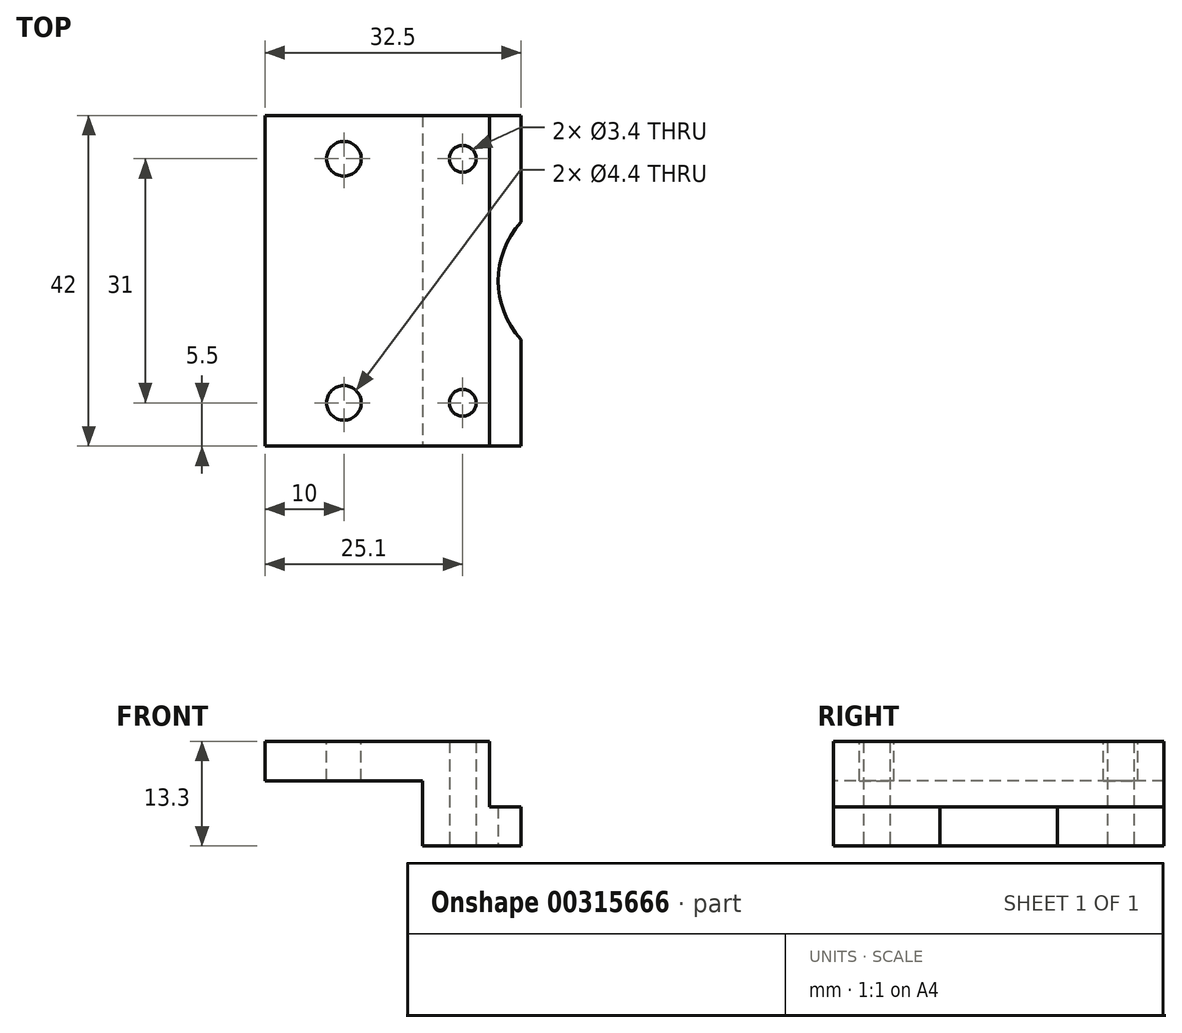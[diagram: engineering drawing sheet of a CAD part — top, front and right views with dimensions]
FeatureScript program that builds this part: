
annotation { "Feature Type Name" : "Feature", "Feature Type Description" : "" }
export const myFeature = defineFeature(function(context is Context, id is Id, definition is map)
    precondition{}
    {
        {
            var Q0;
            Q0=qCreatedBy(makeId("Front.planeOp"),FACE);
            var sketch = newSketch(context, id + "F0", { "sketchPlane" : qUnion([Q0])});
            skLineSegment(sketch, "E0", {"start": v(8.5, 13.3) * mm, "end": v(8.5, 5) * mm});
            skLineSegment(sketch, "E1", {"start": v(8.5, 5) * mm, "end": v(12.5, 5) * mm});
            skLineSegment(sketch, "E2", {"start": v(12.5, 5) * mm, "end": v(12.5, 0) * mm});
            skLineSegment(sketch, "E3", {"start": v(12.5, 0) * mm, "end": v(0, 0) * mm});
            skLineSegment(sketch, "E4", {"start": v(0, 0) * mm, "end": v(0, 13.3) * mm});
            skLineSegment(sketch, "E5", {"start": v(0, 13.3) * mm, "end": v(8.5, 13.3) * mm});
            skSolve(sketch);
        }
        {
            var Q0;
            Q0=qSketchRegion(id+"F0",true);
            extrude(context, id + "F1", {"entities" : qUnion([Q0]), "oppositeDirection" : true, "depth" : 42 * mm});
        }
        {
            var Q0;
            Q0=makeQuery(id+"F1.opExtrude","SWEPT_FACE",FACE,{"disambiguationData":[OSD([sQuery(id+"F0.wireOp",EDGE,"E3")])]});
            var sketch = newSketch(context, id + "F2", { "sketchPlane" : qUnion([Q0])});
            skCircle(sketch, "E6", {"center": v(5.1, -5.5) * mm, "radius": 1.7 * mm});
            skCircle(sketch, "E7", {"center": v(5.1, -36.5) * mm, "radius": 1.7 * mm});
            skCircle(sketch, "E8", {"center": v(20.6, -21) * mm, "radius": 11 * mm});
            skLineSegment(sketch, "E9", {"start": v(0, -21) * mm, "end": v(12.5, -21) * mm, "construction": true});
            skSolve(sketch);
        }
        {
            var Q0;
            Q0=qSketchRegion(id+"F2",true);
            extrude(context, id + "F3", {"entities" : qUnion([Q0]), "operationType" : NewBodyOperationType.REMOVE, "endBound" : BoundingType.THROUGH_ALL, "oppositeDirection" : true, "depth" : 25 * mm});
        }
        {
            var Q0;
            Q0=makeQuery(id+"F1.opExtrude","SWEPT_FACE",FACE,{"disambiguationData":[OSD([sQuery(id+"F0.wireOp",EDGE,"E4")])]});
            var sketch = newSketch(context, id + "F4", { "sketchPlane" : qUnion([Q0])});
            skLineSegment(sketch, "E10.bottom", {"start": v(-42, 13.3) * mm, "end": v(0, 13.3) * mm});
            skLineSegment(sketch, "E10.top", {"start": v(-42, 8.3) * mm, "end": v(0, 8.3) * mm});
            skLineSegment(sketch, "E10.left", {"start": v(-42, 13.3) * mm, "end": v(-42, 8.3) * mm});
            skLineSegment(sketch, "E10.right", {"start": v(0, 13.3) * mm, "end": v(0, 8.3) * mm});
            skSolve(sketch);
        }
        {
            var Q0;
            Q0=qSketchRegion(id+"F4",true);
            extrude(context, id + "F5", {"entities" : qUnion([Q0]), "operationType" : NewBodyOperationType.ADD, "depth" : 20 * mm});
        }
        {
            var Q0;
            Q0=makeQuery(id+"F5.boolean.opBoolean","MERGE",FACE,{"derivedFrom":[makeQuery(id+"F1.opExtrude","SWEPT_FACE",FACE,{"disambiguationData":[OSD([sQuery(id+"F0.wireOp",EDGE,"E5")])]}),makeQuery(id+"F5.opExtrude","SWEPT_FACE",FACE,{"disambiguationData":[OSD([sQuery(id+"F4.wireOp",EDGE,"E10.bottom")])]})]});
            var sketch = newSketch(context, id + "F6", { "sketchPlane" : qUnion([Q0])});
            skCircle(sketch, "E11", {"center": v(-10, 36.5) * mm, "radius": 2.2 * mm});
            skCircle(sketch, "E12", {"center": v(-10, 5.5) * mm, "radius": 2.2 * mm});
            skPoint(sketch, "E13", {"position": v(5.1, 36.5) * mm});
            skPoint(sketch, "E14", {"position": v(5.1, 5.5) * mm});
            skSolve(sketch);
        }
        {
            var Q0;
            Q0=qSketchRegion(id+"F6",true);
            extrude(context, id + "F7", {"entities" : qUnion([Q0]), "operationType" : NewBodyOperationType.REMOVE, "oppositeDirection" : true, "depth" : 25 * mm});
        }
        {
            var Q0;
            Q0=makeQuery(id+"F5.boolean.opBoolean","MERGE",FACE,{"derivedFrom":[makeQuery(id+"F1.opExtrude","SWEPT_FACE",FACE,{"disambiguationData":[OSD([sQuery(id+"F0.wireOp",EDGE,"E5")])]}),makeQuery(id+"F5.opExtrude","SWEPT_FACE",FACE,{"disambiguationData":[OSD([sQuery(id+"F4.wireOp",EDGE,"E10.bottom")])]})]});
            var sketch = newSketch(context, id + "F8", { "sketchPlane" : qUnion([Q0])});
            skText(sketch, "E15", { "text": "L", "fontName": "OpenSans-Bold.ttf"});
            const initialGuessF8  = {"E15": [-0.02, 0.0315, 0, -1, 0.0285]};
            skSetInitialGuess(sketch, initialGuessF8);
            skSolve(sketch);
        }
        {
            var Q0;
            Q0=qSketchRegion(id+"F8",true);
            extrude(context, id + "F9", {"entities" : qUnion([Q0]), "operationType" : NewBodyOperationType.ADD, "depth" : 1 * mm});
        }
        {
            var Q0;
            Q0=makeQuery(id+"F9.opExtrude","CAP_FACE",FACE,{"disambiguationData":[OSD([sQuery(id+"F8.wireOp",EDGE,"E15.sketch_text.stroke-0"),sQuery(id+"F8.wireOp",EDGE,"E15.sketch_text.stroke-1"),sQuery(id+"F8.wireOp",EDGE,"E15.sketch_text.stroke-2"),sQuery(id+"F8.wireOp",EDGE,"E15.sketch_text.stroke-3"),sQuery(id+"F8.wireOp",EDGE,"E15.sketch_text.stroke-4"),sQuery(id+"F8.wireOp",EDGE,"E15.sketch_text.stroke-5")])],"isStart":false});
            extrude(context, id + "F10", {"entities" : qUnion([Q0]), "operationType" : NewBodyOperationType.REMOVE, "oppositeDirection" : true, "depth" : 1 * mm});
        }
    });
